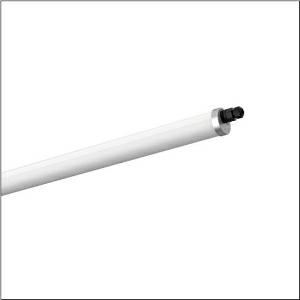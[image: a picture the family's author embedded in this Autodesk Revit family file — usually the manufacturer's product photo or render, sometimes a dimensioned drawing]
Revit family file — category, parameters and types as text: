
# Revit family: monsun_r__31_tube_51ft107n480a_b45d
name_source: partatom
category: Lighting Fixtures
units: mm (PartAtom-declared; Revit-internal decimal feet)

## family parameters
Cut with Voids When Loaded = No
Host = Face
Light Source = No
Part Type = Normal
Room Calculation Point = No
Round Connector Dimension = Use Diameter
Shared = No

## types (1)
- Monsun® 31 Tube (1 x LED, 8000 lm, 50 W, 4000K)
    Apparent Load = 50 VA
    CIE Flux Codes = 42 71 89 91 100
    Color Rendering = 80
    Color Temperature = 4000K
    Default Elevation = 1800 mm
    Description = Monsun® 31 Tube, tubular luminaire, primary optical cover: diffuser, of PMMA, light emission: direct distribution, primary light characteristic: symmetric, installation type: suspended mounting, surface-mounted, LED, rated luminous flux: 8.000lm, luminous efficacy: 160lm/W, light colour: 840, colour temperature: 4000K, control gear: ON/OFF, with with 1 terminal, 3-pole, max. 2.5mm², through-wiring: 3x 1.5mm², mains connection: 220..240V, AC, 50/60Hz, rated input power: 50W, housing, cylindrical, of PMMA, semi-transparent, matt white, with luminaire and ceiling fastening, V4A, mounting with brackets of stainless steel, length: 1.560mm, diameter: 75mm, end cap, of stainless steel (V4A), protection rating (complete): IP67/IP69K, insulation class (complete): insulation class I (protective earthing), certification: CE, UKCA, impact resistance: IK07, permissible operating ambient temperature: -20..+40°C, corresponds to IFS (International Featured Standards) requirements for safety and quality in the food industry, usage in unprotected outdoor areas possible with horizontal mounting, contact your sales advisor before using the luminaires in applications with unclear chemical exposure, large temperature fluctuations or condensation-forming humidity, packaging unit: 1 piece
    Height = 83 mm
    Lamp = 1 x LED
    Lamp Light Flux = 8000 lm
    Lamp Power = 50 W
    Lamp count = 1
    Length = 1560 mm
    Luminous efficacy = 160 lm/W
    Manufacturer = Siteco
    ModVariant = No
    Model = 51FT107N480A
    Mounting Place = Ceiling
    Mounting Type = Pendant
    Number of Poles = 1
    OnlyDefault = Yes
    Power Factor = 1
    Product Name = Monsun® 31 Tube
    Product group = tubular luminaire
    ProductGroupID = 906
    Protection Class = Protection class I
    RLX_Detail_Level = 1
    RLX_Emergency_Light_Flux = 0 lm
    RLX_Emergency_Type = 0
    RLX_Emergency_Type_DB = No
    RlxData = <blob elided: 25385 chars, md5=6616ca0a>
    Socket = socket
    Standby Power = 0 W
    System Light Flux = 8000 lm
    System Power = 50 W
    Type Comments = Product without accessories
    Type Image = l_1228461.jpg
    URL = http://relux.com
    VarID = ---
    Voltage = 0 V
    Weight = 0.00 kg
    Width = 75 mm

## geometry (parser evidence)
native form markers: Blend x4, Sweep x13
no freeform markers — native parametric forms only
